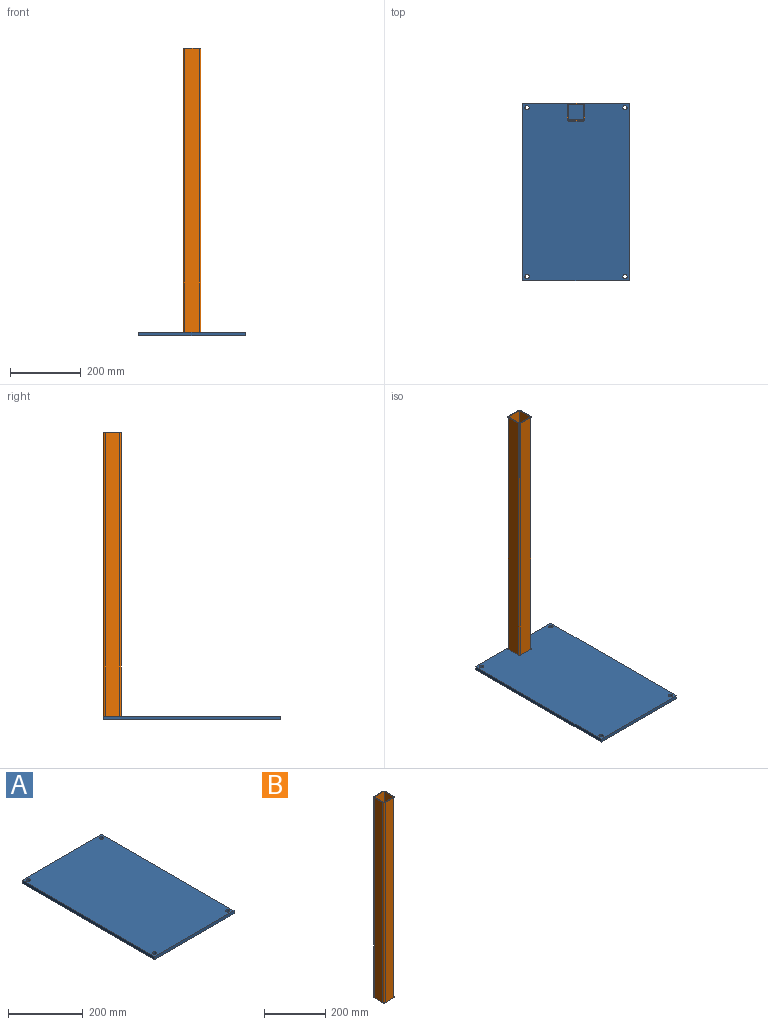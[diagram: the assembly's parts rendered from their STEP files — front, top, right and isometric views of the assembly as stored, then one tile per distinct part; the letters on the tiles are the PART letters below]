
ASSEMBLY  parts=2 mates=1
PART A: 10 faces, bbox 300x500x10 mm
  f0: plane 300x10mm, normal (0,-1,0), area 3000mm2, adj f1,f7,f8,f9
  f1: plane 500x10mm, normal (1,0,0), area 5000mm2, adj f0,f2,f8,f9
  f2: plane 300x10mm, normal (0,1,0), area 3000mm2, adj f1,f7,f8,f9
  f3: cylinder r=6mm len=12mm, axis (0,0,-1), area 377mm2, adj f8,f9
  f4: cylinder r=6mm len=12mm, axis (0,0,-1), area 377mm2, adj f8,f9
  f5: cylinder r=6mm len=12mm, axis (0,0,-1), area 377mm2, adj f8,f9
  f6: cylinder r=6mm len=12mm, axis (0,0,-1), area 377mm2, adj f8,f9
  f7: plane 500x10mm, normal (-1,0,0), area 5000mm2, adj f0,f2,f8,f9
  f8: plane 500x300mm, normal (0,0,1), area 149547.6mm2, adj f0,f1,f2,f3,f4,f5,f6,f7
  f9: plane 500x300mm, normal (0,0,-1), area 149547.6mm2, adj f0,f1,f2,f3,f4,f5,f6,f7
PART B: 14 faces, bbox 50x50x800 mm
  f0: plane 800x40mm, normal (0,-1,0), area 32000mm2, adj f8,f9,f10,f13
  f1: plane 800x40mm, normal (1,0,0), area 32000mm2, adj f8,f9,f10,f11
  f2: plane 800x40mm, normal (0,1,0), area 32000mm2, adj f8,f9,f11,f12
  f3: plane 800x44mm, normal (0,1,0), area 35200mm2, adj f4,f6,f8,f9
  f4: plane 800x44mm, normal (1,0,0), area 35200mm2, adj f3,f5,f8,f9
  f5: plane 800x44mm, normal (0,-1,0), area 35200mm2, adj f4,f6,f8,f9
  f6: plane 800x44mm, normal (-1,0,0), area 35200mm2, adj f3,f5,f8,f9
  f7: plane 800x40mm, normal (-1,0,0), area 32000mm2, adj f8,f9,f12,f13
  f8: plane 50x50mm, normal (0,0,1), area 542.5mm2, adj f0,f1,f2,f3,f4,f5,f6,f7
  f9: plane 50x50mm, normal (0,0,-1), area 542.5mm2, adj f0,f1,f2,f3,f4,f5,f6,f7
  f10: cylinder r=5mm len=800mm, axis (0,0,1), area 6283.2mm2, adj f0,f1,f8,f9
  f11: cylinder r=5mm len=800mm, axis (0,0,-1), area 6283.2mm2, adj f1,f2,f8,f9
  f12: cylinder r=5mm len=800mm, axis (0,0,1), area 6283.2mm2, adj f2,f7,f8,f9
  f13: cylinder r=5mm len=800mm, axis (0,0,-1), area 6283.2mm2, adj f0,f7,f8,f9
PLACE A t=(0.33,0.19,-5)mm
PLACE B t=(0.33,225.19,5)mm
MATE fastened B.f9 <-> A.f8  axis (0,0,-1) through (0.33,250.19,5)mm
